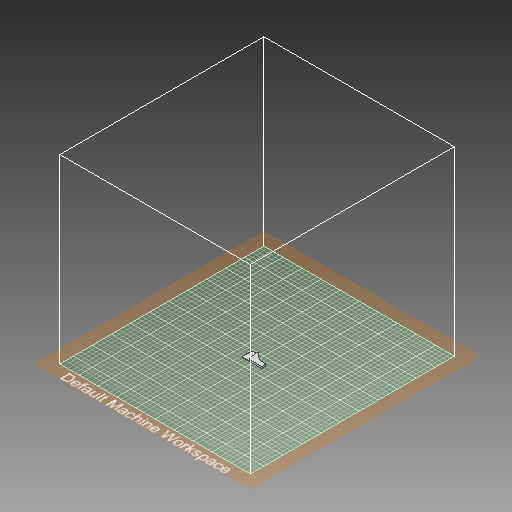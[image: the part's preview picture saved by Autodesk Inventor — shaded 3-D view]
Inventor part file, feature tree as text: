
AUTODESK INVENTOR PART (.ipt)
format: ipt  version: 2019 (Build 230136000, 136)  size: 270,336 bytes
history: native  units: in
note: dims shown in document units (in); Inventor stores cm internally (conversion verified against a paired STEP export)
features: extrude x2, sketch x2, fillet x1, projected_geometry x1
ambient origin geometry x8: Origin, YZ Plane, XZ Plane, XY Plane, X Axis, Y Axis, Z Axis, Center Point
bodies: Solid1 (feature_tree)
feature tree (6):
  extrude  "Extrusion1"  Depth=0.1181in
  extrude  "Extrusion2"  Depth=0.0787in
  fillet  "Fillet1"  [1 undecoded]
  sketch  "Sketch1"  dims[d0=1.1818in d1=0.8858in d2=0.6788in d3=0.3877in d4=0.5497in d5=1.0271in d6=0.5212in d7=0.1181in d8=0.0in d9=0.4429in]
  sketch  "Sketch2"  dims[d10=0.0394in d11=0.0in d12=0.0787in]
  projected_geometry  "Projected Loop1"
note: 1 required parameter value undecoded (feature->parameter linkage not recoverable at this tier; creation-order binding heuristic only, values carry confidence <= 0.55)
